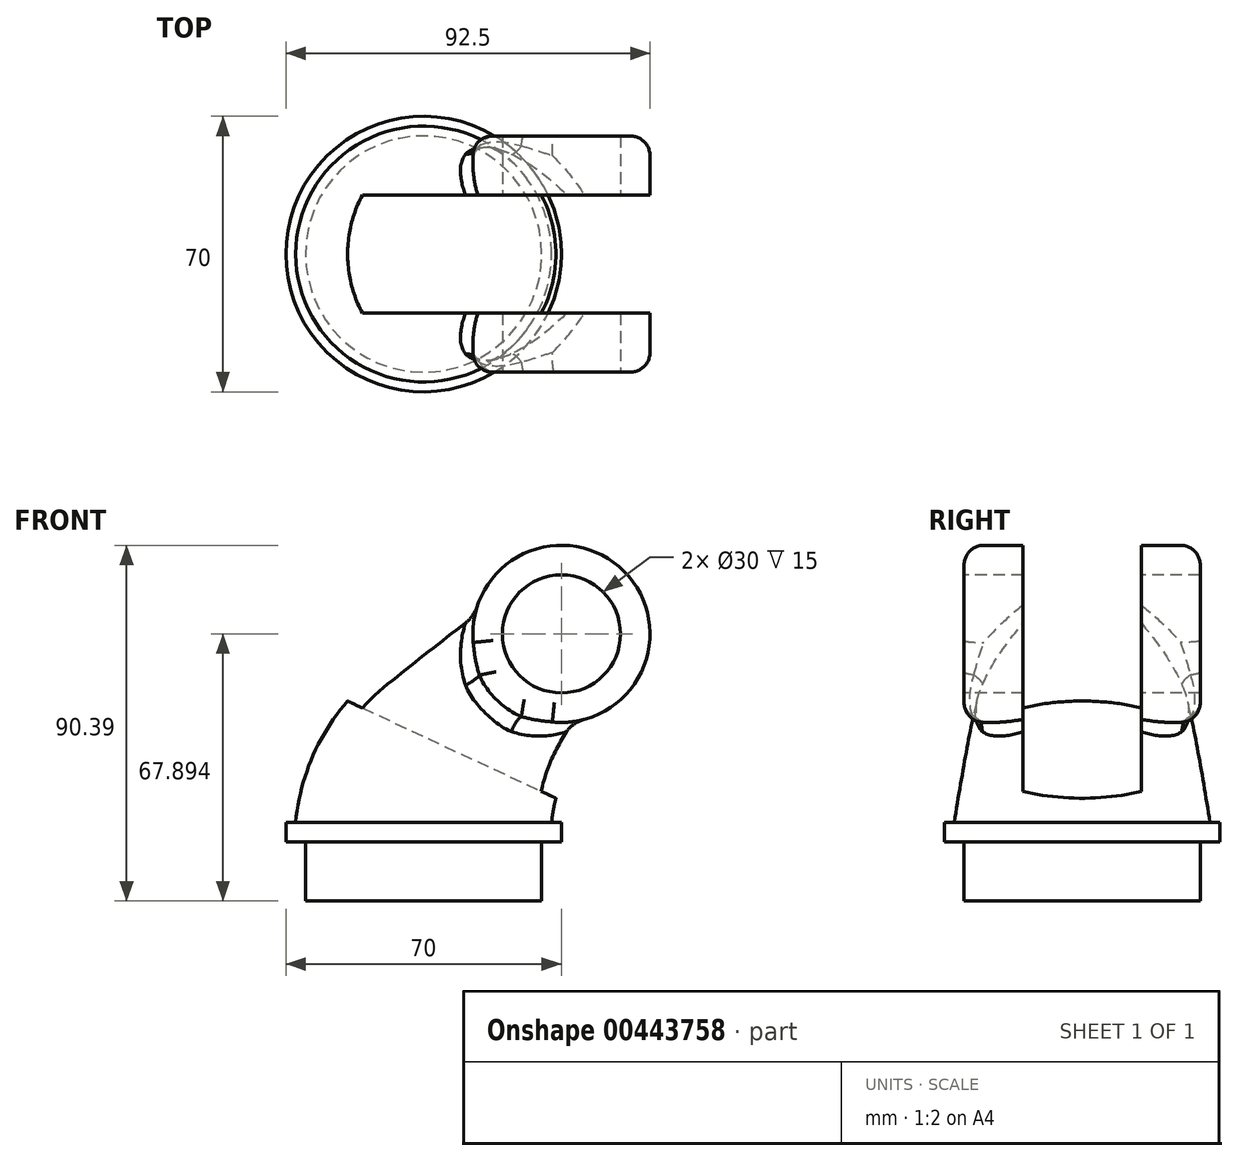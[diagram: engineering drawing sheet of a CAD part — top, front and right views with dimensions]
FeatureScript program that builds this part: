
annotation { "Feature Type Name" : "Feature", "Feature Type Description" : "" }
export const myFeature = defineFeature(function(context is Context, id is Id, definition is map)
    precondition{}
    {
        {
            var Q0;
            Q0=qCreatedBy(makeId("Top.planeOp"),FACE);
            var sketch = newSketch(context, id + "F0", { "sketchPlane" : qUnion([Q0])});
            skCircle(sketch, "E0", {"center": v(0, 0) * mm, "radius": 35 * mm});
            skSolve(sketch);
        }
        {
            var Q0;
            Q0 = qSketchRegion(id + "F0", true);
            extrude(context, id + "F1", {"entities" : qUnion([Q0]), "depth" : 5 * mm});
        }
        {
            var Q0;
            Q0=qCreatedBy(makeId("Front.planeOp"),FACE);
            var sketch = newSketch(context, id + "F2", { "sketchPlane" : qUnion([Q0])});
            skArc(sketch, "E1", {"start": v(17.6, 38.3) * mm, "mid": v(5.55, 23.37) * mm, "end": v(0, 5) * mm});
            skLineSegment(sketch, "E2", {"start": v(17.6, 38.3) * mm, "end": v(35, 52.9) * mm});
            skSolve(sketch);
        }
        {
            var Q0;
            Q0=sQuery(id+"F2.wireOp",EDGE,"E2");
            var Q1;
            Q1=sQuery(id+"F2.wireOp",VERTEX,"E2.end");
            cPlane(context, id + "F3", {"entities" : qUnion([Q0, Q1]), "cplaneType" : CPlaneType.LINE_POINT, "offset" : 25 * mm, "width" : 150 * mm, "height" : 150 * mm});
        }
        {
            var Q0;
            Q0=qCreatedBy(id+"F3.planeOp",FACE);
            var sketch = newSketch(context, id + "F4", { "sketchPlane" : qUnion([Q0])});
            skCircle(sketch, "E3", {"center": v(0, 18.02) * mm, "radius": 22.5 * mm});
            skSolve(sketch);
        }
        {
            var Q0;
            Q0=makeQuery(id+"F1.opExtrude","CAP_FACE",FACE,{"disambiguationData":[OSD([sQuery(id+"F0.wireOp",EDGE,"E0")])],"isStart":false});
            var sketch = newSketch(context, id + "F5", { "sketchPlane" : qUnion([Q0])});
            skCircle(sketch, "E4", {"center": v(0, 0) * mm, "radius": 32.5 * mm});
            skSolve(sketch);
        }
        {
            var Q0;
            Q0=qCreatedBy(makeId("Front.planeOp"),FACE);
            var sketch = newSketch(context, id + "F6", { "sketchPlane" : qUnion([Q0])});
            skArc(sketch, "E5", {"start": v(-13.25, 41.78) * mm, "mid": v(-26.5, 25.3) * mm, "end": v(-32.5, 5) * mm});
            skLineSegment(sketch, "E6", {"start": v(-13.25, 41.78) * mm, "end": v(20.54, 70.13) * mm});
            skSolve(sketch);
        }
        {
            var Q0;
            Q0=qCreatedBy(makeId("Front.planeOp"),FACE);
            var sketch = newSketch(context, id + "F7", { "sketchPlane" : qUnion([Q0])});
            skArc(sketch, "E7", {"start": v(48.46, 34.82) * mm, "mid": v(37.6, 21.45) * mm, "end": v(32.5, 5) * mm});
            skLineSegment(sketch, "E8", {"start": v(48.46, 34.82) * mm, "end": v(49.46, 35.66) * mm});
            skSolve(sketch);
        }
        {
            var Q1;
            Q1=makeQuery(id+"F5.imprint","IMPRINT",FACE,{"disambiguationData":[TD([[makeQuery(id+"F5.imprint","IMPRINT",EDGE,{"derivedFrom":sQuery(id+"F5.wireOp",EDGE,"E4")}),1.0]])]});
            var Q2;
            Q2=makeQuery(id+"F4.imprint","IMPRINT",FACE,{"disambiguationData":[TD([[makeQuery(id+"F4.imprint","IMPRINT",EDGE,{"derivedFrom":sQuery(id+"F4.wireOp",EDGE,"E3")}),1.0]])]});
            var Q3;
            Q3 = qConstructionFilter(qBodyType(qCreatedBy(id + "F6" ,EDGE), BodyType.WIRE), ConstructionObject.NO);
            var Q4;
            Q4 = qConstructionFilter(qBodyType(qCreatedBy(id + "F7" ,EDGE), BodyType.WIRE), ConstructionObject.NO);
            loft(context, id + "F8", {"operationType" : NewBodyOperationType.ADD, "addGuides" : true, "sheetProfilesArray" : [{ "sheetProfileEntities" : qUnion([Q1]) }, { "sheetProfileEntities" : qUnion([Q2]) }], "guidesArray" : [{ "guideEntities" : qUnion([Q3]), "guideDerivativeType" : LoftGuideDerivativeType.DEFAULT, "guideDerivativeMagnitude" : 1 }, { "guideEntities" : qUnion([Q4]), "guideDerivativeType" : LoftGuideDerivativeType.DEFAULT, "guideDerivativeMagnitude" : 1 }]});
        }
        {
            var Q0;
            Q0=qCreatedBy(makeId("Front.planeOp"),FACE);
            var sketch = newSketch(context, id + "F9", { "sketchPlane" : qUnion([Q0])});
            skCircle(sketch, "E9", {"center": v(35, 52.9) * mm, "radius": 22.5 * mm});
            skSolve(sketch);
        }
        {
            var Q0;
            Q0 = qSketchRegion(id + "F9", true);
            extrude(context, id + "F10", {"entities" : qUnion([Q0]), "operationType" : NewBodyOperationType.ADD, "endBound" : BoundingType.SYMMETRIC, "depth" : 60 * mm});
        }
        {
            var Q0;
            Q0=makeQuery(id+"F10.boolean.opBoolean","INTERSECT",EDGE,{"disambiguationData":[OD(0.0)],"derivedFrom":[makeQuery(id+"F8.opLoft","SWEPT_FACE",FACE,{"disambiguationData":[OSD([sQuery(id+"F4.wireOp",EDGE,"E3"),sQuery(id+"F5.wireOp",EDGE,"E4"),sQuery(id+"F6.wireOp",VERTEX,"E6.start"),sQuery(id+"F6.wireOp",EDGE,"E5"),sQuery(id+"F6.wireOp",EDGE,"E6"),sQuery(id+"F7.wireOp",VERTEX,"E8.start"),sQuery(id+"F7.wireOp",EDGE,"E7"),sQuery(id+"F7.wireOp",EDGE,"E8")])]}),makeQuery(id+"F10.opExtrude","SWEPT_FACE",FACE,{"disambiguationData":[OSD([sQuery(id+"F9.wireOp",EDGE,"E9")])]})]});
            var Q1;
            Q1=makeQuery(id+"F10.boolean.opBoolean","INTERSECT",EDGE,{"disambiguationData":[OD(1.0)],"derivedFrom":[makeQuery(id+"F8.opLoft","SWEPT_FACE",FACE,{"disambiguationData":[OSD([sQuery(id+"F4.wireOp",EDGE,"E3"),sQuery(id+"F5.wireOp",EDGE,"E4"),sQuery(id+"F6.wireOp",VERTEX,"E6.start"),sQuery(id+"F6.wireOp",EDGE,"E5"),sQuery(id+"F6.wireOp",EDGE,"E6"),sQuery(id+"F7.wireOp",VERTEX,"E8.start"),sQuery(id+"F7.wireOp",EDGE,"E7"),sQuery(id+"F7.wireOp",EDGE,"E8")])]}),makeQuery(id+"F10.opExtrude","SWEPT_FACE",FACE,{"disambiguationData":[OSD([sQuery(id+"F9.wireOp",EDGE,"E9")])]})]});
            fillet(context, id + "F11", {"entities" : qUnion([Q0, Q1]), "radius" : 5 * mm, "tangentPropagation" : true, "allowEdgeOverflow" : false});
        }
        {
            var Q0;
            Q0=makeQuery(id+"F10.opExtrude","CAP_EDGE",EDGE,{"disambiguationData":[OSD([sQuery(id+"F9.wireOp",EDGE,"E9")])],"isStart":false});
            var Q1;
            Q1=makeQuery(id+"F10.opExtrude","CAP_FACE",FACE,{"disambiguationData":[OSD([sQuery(id+"F9.wireOp",EDGE,"E9")])],"isStart":true});
            fillet(context, id + "F12", {"entities" : qUnion([Q0, Q1]), "radius" : 5 * mm, "tangentPropagation" : true, "allowEdgeOverflow" : false});
        }
        {
            var Q0;
            Q0=makeQuery(id+"F10.opExtrude","CAP_FACE",FACE,{"disambiguationData":[OSD([sQuery(id+"F9.wireOp",EDGE,"E9")])],"isStart":false});
            var sketch = newSketch(context, id + "F13", { "sketchPlane" : qUnion([Q0])});
            skCircle(sketch, "E10", {"center": v(35, 52.9) * mm, "radius": 15 * mm});
            skSolve(sketch);
        }
        {
            var Q0;
            Q0 = qSketchRegion(id + "F13", true);
            extrude(context, id + "F14", {"entities" : qUnion([Q0]), "operationType" : NewBodyOperationType.REMOVE, "endBound" : BoundingType.THROUGH_ALL, "oppositeDirection" : true, "depth" : 25 * mm});
        }
        {
            var Q0;
            Q0=qCreatedBy(makeId("Front.planeOp"),FACE);
            var sketch = newSketch(context, id + "F15", { "sketchPlane" : qUnion([Q0])});
            skLineSegment(sketch, "E11", {"start": v(-104.18, 75.4) * mm, "end": v(57.5, 0) * mm});
            skLineSegment(sketch, "E12", {"start": v(57.5, 75.4) * mm, "end": v(57.5, 0) * mm});
            skLineSegment(sketch, "E13", {"start": v(-104.18, 75.4) * mm, "end": v(57.5, 75.4) * mm});
            skSolve(sketch);
        }
        {
            var Q0;
            Q0 = qSketchRegion(id + "F15", true);
            extrude(context, id + "F16", {"entities" : qUnion([Q0]), "operationType" : NewBodyOperationType.REMOVE, "endBound" : BoundingType.SYMMETRIC, "oppositeDirection" : true, "depth" : 30 * mm});
        }
        {
            var Q0;
            Q0=qCreatedBy(makeId("Front.planeOp"),FACE);
            var sketch = newSketch(context, id + "F17", { "sketchPlane" : qUnion([Q0])});
            skLineSegment(sketch, "E14.bottom", {"start": v(0, 0) * mm, "end": v(-30, 0) * mm});
            skLineSegment(sketch, "E14.top", {"start": v(0, -15) * mm, "end": v(-30, -15) * mm});
            skLineSegment(sketch, "E14.left", {"start": v(0, 0) * mm, "end": v(0, -15) * mm});
            skLineSegment(sketch, "E14.right", {"start": v(-30, 0) * mm, "end": v(-30, -15) * mm});
            skSolve(sketch);
        }
        {
            var Q0;
            Q0=makeQuery(id+"F17.imprint","IMPRINT",FACE,{"disambiguationData":[TD([[makeQuery(id+"F17.imprint","IMPRINT",EDGE,{"derivedFrom":sQuery(id+"F17.wireOp",EDGE,"E14.bottom")}),1.0]])]});
            var Q1;
            Q1=sQuery(id+"F17.wireOp",EDGE,"E14.left");
            revolve(context, id + "F18", {"operationType" : NewBodyOperationType.ADD, "entities" : qUnion([Q0]), "axis" : qUnion([Q1]), "revolveType" : RevolveType.FULL});
        }
    });
